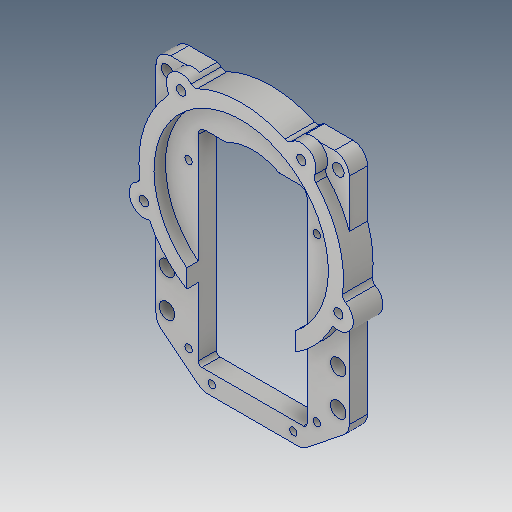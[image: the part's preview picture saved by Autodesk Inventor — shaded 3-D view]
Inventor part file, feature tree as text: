
AUTODESK INVENTOR PART (.ipt)
format: ipt  version: 2020.5 (Build 245400000, 400)  size: 502,272 bytes
history: native  units: mm
features: sketch x11, extrude x10, projected_geometry x10, fillet x5, other x1
ambient origin geometry x8: Origin, YZ Plane, XZ Plane, XY Plane, X Axis, Y Axis, Z Axis, Center Point
bodies: Body1 (feature_tree)
feature tree (37):
  other  "솔리드1"
  extrude  "돌출1"  Depth=47.07mm
  extrude  "돌출2"  Depth=55.2mm
  extrude  "돌출3"  Depth=8.0mm
  extrude  "돌출4"  Depth=50.0mm TaperAngle=360.0deg
  extrude  "돌출5"  Depth=3.1mm TaperAngle=0.0deg
  extrude  "돌출6"  Depth=55.2mm
  extrude  "돌출7"  Depth=8.0mm
  fillet  "모깎기1"  [1 undecoded]
  fillet  "모깎기2"  Radius=14.7mm
  fillet  "모깎기3"  [1 undecoded]
  fillet  "모깎기4"  Radius=14.7mm
  extrude  "돌출8"  Depth=3.1mm TaperAngle=0.0deg
  extrude  "돌출9"  Depth=74.0mm
  fillet  "모깎기5"  Radius=52.2mm
  sketch  "스케치10"
  extrude  "돌출10"  Depth=26.1mm
  sketch  "스케치1"
  sketch  "스케치2"
  sketch  "스케치3"
  projected_geometry  "투영된 루프1"
  sketch  "스케치4"
  projected_geometry  "투영된 루프2"
  projected_geometry  "투영된 루프3"
  sketch  "스케치5"
  sketch  "스케치6"
  projected_geometry  "투영된 루프4"
  sketch  "스케치7"
  sketch  "스케치8"
  sketch  "스케치9"
  projected_geometry  "투영된 루프5"
  projected_geometry  "투영된 루프6"
  projected_geometry  "투영된 루프7"
  projected_geometry  "투영된 루프8"
  projected_geometry  "투영된 루프9"
  sketch  "스케치11"
  projected_geometry  "투영된 루프10"
note: 2 required parameter values undecoded (feature->parameter linkage not recoverable at this tier; creation-order binding heuristic only, values carry confidence <= 0.55)
